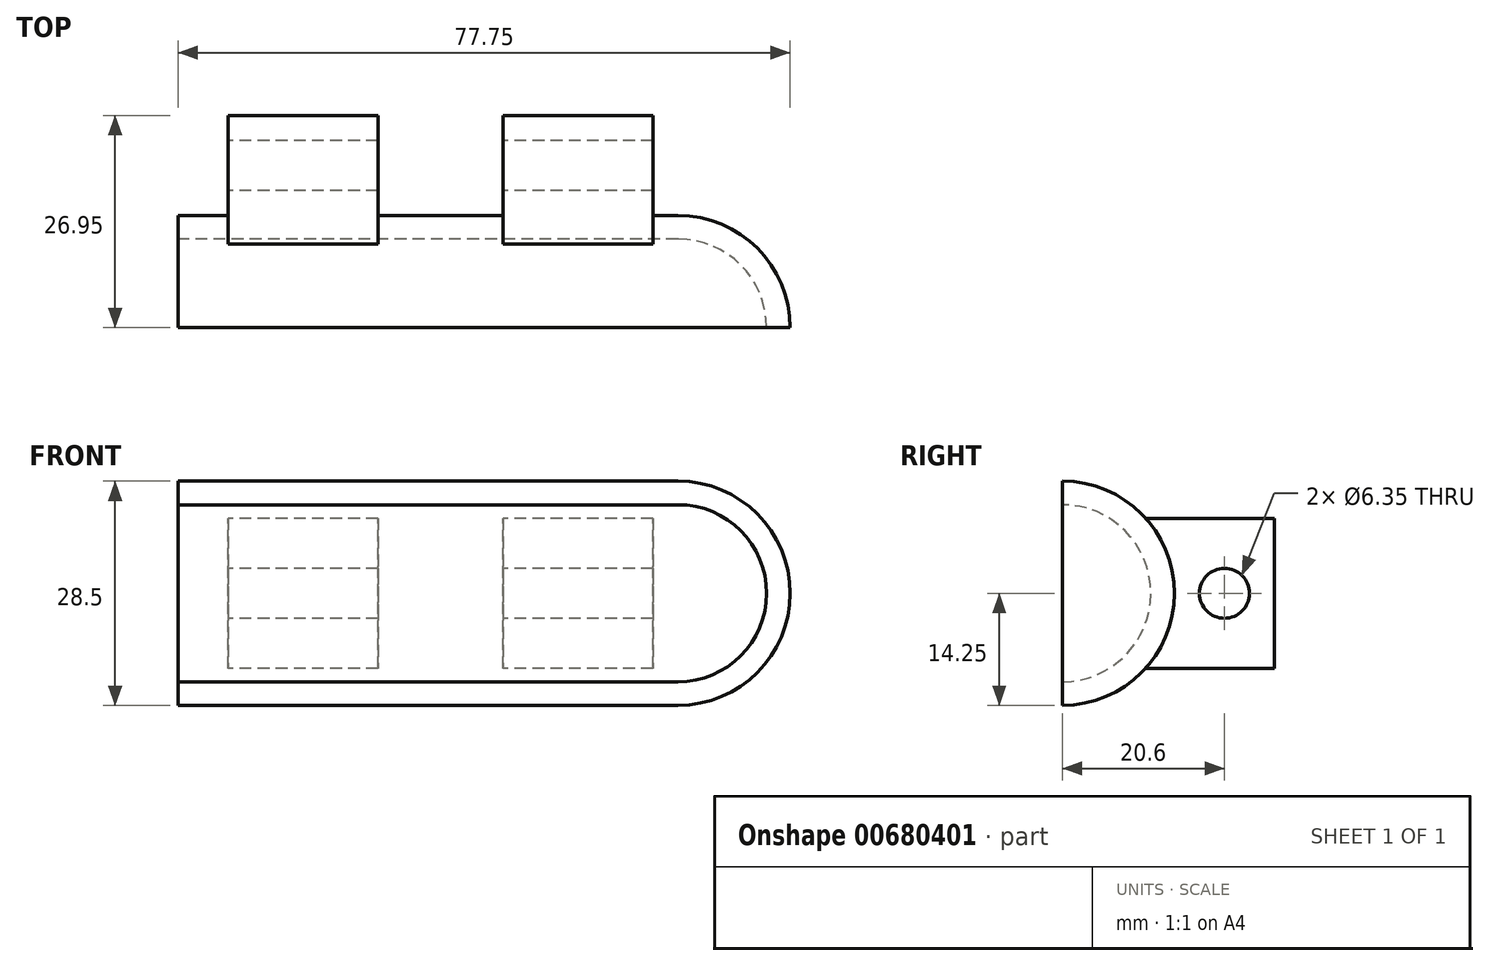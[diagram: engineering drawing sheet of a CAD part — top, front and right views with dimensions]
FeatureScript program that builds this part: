
annotation { "Feature Type Name" : "Feature", "Feature Type Description" : "" }
export const myFeature = defineFeature(function(context is Context, id is Id, definition is map)
    precondition{}
    {
        {
            var Q0;
            Q0=qCreatedBy(makeId("Front.planeOp"),FACE);
            var sketch = newSketch(context, id + "F0", { "sketchPlane" : qUnion([Q0])});
            skArc(sketch, "E0", {"start": v(31.75, -11.25) * mm, "mid": v(39.7, -7.95) * mm, "end": v(43, 0) * mm});
            skLineSegment(sketch, "E1", {"start": v(0, 11.25) * mm, "end": v(0, -11.25) * mm, "construction": true});
            skLineSegment(sketch, "E2", {"start": v(0, 0) * mm, "end": v(56, 0) * mm, "construction": true});
            skLineSegment(sketch, "E3", {"start": v(31.75, -11.25) * mm, "end": v(0, -11.25) * mm});
            skPoint(sketch, "E4.MirrorCS.end.orphan", {"position": v(0, 11.25) * mm});
            skPoint(sketch, "E5.MirrorCS.end.orphan", {"position": v(0, -11.25) * mm});
            skLineSegment(sketch, "E6.MirrorCS", {"start": v(-31.75, -11.25) * mm, "end": v(0, -11.25) * mm});
            skLineSegment(sketch, "E7", {"start": v(-31.75, -14.25) * mm, "end": v(-31.75, -11.25) * mm});
            skLineSegment(sketch, "E8", {"start": v(-31.75, -14.25) * mm, "end": v(31.75, -14.25) * mm});
            skArc(sketch, "E9", {"start": v(31.75, -14.25) * mm, "mid": v(41.83, -10.08) * mm, "end": v(46, 0) * mm});
            skLineSegment(sketch, "E10", {"start": v(43, 0) * mm, "end": v(46, 0) * mm});
            skSolve(sketch);
        }
        {
            var Q0;
            Q0 = qSketchRegion(id + "F0", true);
            var Q1;
            Q1=sQuery(id+"F0.wireOp",EDGE,"E2");
            revolve(context, id + "F1", {"entities" : qUnion([Q0]), "axis" : qUnion([Q1]), "revolveType" : RevolveType.ONE_DIRECTION, "angle" : 180 * degree});
        }
        {
            var Q0;
            Q0=qCreatedBy(makeId("Right.planeOp"),FACE);
            var sketch = newSketch(context, id + "F2", { "sketchPlane" : qUnion([Q0])});
            skLineSegment(sketch, "E11", {"start": v(26.95, -8.53) * mm, "end": v(26.95, 11.07) * mm});
            skSolve(sketch);
        }
        {
            var Q0;
            Q0 = qBodyType(qCreatedBy(id + "F2" ,EDGE), BodyType.WIRE);
            var Q1;
            Q1=qCreatedBy(makeId("Front.planeOp"),FACE);
            cPlane(context, id + "F3", {"entities" : qUnion([Q0, Q1]), "cplaneType" : CPlaneType.LINE_ANGLE, "offset" : 25.4 * mm, "angle" : 0 * degree, "width" : 152.4 * mm, "height" : 152.4 * mm});
        }
        {
            var Q0;
            Q0=qCreatedBy(id+"F3.planeOp",FACE);
            var sketch = newSketch(context, id + "F4", { "sketchPlane" : qUnion([Q0])});
            skLineSegment(sketch, "E12.bottom", {"start": v(-9.53, 9.52) * mm, "end": v(-28.58, 9.52) * mm});
            skLineSegment(sketch, "E12.top", {"start": v(-9.53, 0) * mm, "end": v(-28.58, 0) * mm, "construction": true});
            skLineSegment(sketch, "E12.left", {"start": v(-9.53, 0) * mm, "end": v(-9.53, 9.52) * mm});
            skLineSegment(sketch, "E12.right", {"start": v(-28.58, 0) * mm, "end": v(-28.58, 9.52) * mm});
            skLineSegment(sketch, "E13", {"start": v(-1.59, 19.02) * mm, "end": v(-1.59, 5.71) * mm, "construction": true});
            skLineSegment(sketch, "E14.MirrorCS", {"start": v(-28.58, 0) * mm, "end": v(-28.58, -9.52) * mm});
            skLineSegment(sketch, "E15.MirrorCS", {"start": v(-9.53, 0) * mm, "end": v(-9.53, -9.53) * mm});
            skLineSegment(sketch, "E16.MirrorCS", {"start": v(-9.53, -9.53) * mm, "end": v(-28.58, -9.53) * mm});
            skLineSegment(sketch, "E17.MirrorCS", {"start": v(6.35, 9.52) * mm, "end": v(25.4, 9.52) * mm});
            skLineSegment(sketch, "E18.MirrorCS", {"start": v(6.35, 0) * mm, "end": v(6.35, 9.53) * mm});
            skLineSegment(sketch, "E19.MirrorCS", {"start": v(25.4, 9.52) * mm, "end": v(25.4, 0) * mm});
            skLineSegment(sketch, "E20.MirrorCS", {"start": v(6.35, -9.53) * mm, "end": v(6.35, 0) * mm});
            skLineSegment(sketch, "E21.MirrorCS", {"start": v(25.4, -9.52) * mm, "end": v(25.4, 0) * mm});
            skLineSegment(sketch, "E22.MirrorCS", {"start": v(6.35, -9.53) * mm, "end": v(25.4, -9.53) * mm});
            skSolve(sketch);
        }
        {
            var Q0;
            Q0=makeQuery(id+"F4.imprint","IMPRINT",FACE,{"disambiguationData":[TD([[makeQuery(id+"F4.imprint","IMPRINT",EDGE,{"derivedFrom":sQuery(id+"F4.wireOp",EDGE,"E17.MirrorCS")}),-1.0]])]});
            var Q1;
            Q1=makeQuery(id+"F4.imprint","IMPRINT",FACE,{"disambiguationData":[TD([[makeQuery(id+"F4.imprint","IMPRINT",EDGE,{"derivedFrom":sQuery(id+"F4.wireOp",EDGE,"E12.bottom")}),1.0]])]});
            var Q2;
            Q2=makeQuery(id+"F1.opRevolve","SWEPT_FACE",FACE,{"disambiguationData":[OSD([sQuery(id+"F0.wireOp",EDGE,"E8")])]});
            extrude(context, id + "F5", {"entities" : qUnion([Q0, Q1]), "operationType" : NewBodyOperationType.ADD, "endBound" : BoundingType.UP_TO_SURFACE, "oppositeDirection" : true, "depth" : 25.4 * mm, "endBoundEntityFace" : qUnion([Q2]), "offsetDistance" : 25.4 * mm});
        }
        {
            var Q0;
            Q0=makeQuery(id+"F5.opExtrude","SWEPT_FACE",FACE,{"disambiguationData":[OSD([sQuery(id+"F4.wireOp",EDGE,"E19.MirrorCS"),sQuery(id+"F4.wireOp",EDGE,"E21.MirrorCS")])]});
            var sketch = newSketch(context, id + "F6", { "sketchPlane" : qUnion([Q0])});
            skLineSegment(sketch, "E23", {"start": v(-26.95, 0) * mm, "end": v(-20.6, 0) * mm, "construction": true});
            skCircle(sketch, "E24", {"center": v(-20.6, 0) * mm, "radius": 3.18 * mm});
            skSolve(sketch);
        }
        {
            var Q0;
            Q0 = qSketchRegion(id + "F6", true);
            extrude(context, id + "F7", {"entities" : qUnion([Q0]), "operationType" : NewBodyOperationType.REMOVE, "endBound" : BoundingType.THROUGH_ALL, "oppositeDirection" : true, "depth" : 25.4 * mm, "offsetDistance" : 25.4 * mm});
        }
    });
